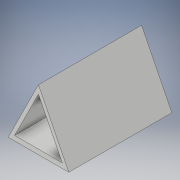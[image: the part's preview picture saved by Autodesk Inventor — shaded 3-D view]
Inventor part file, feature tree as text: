
AUTODESK INVENTOR PART (.ipt)
format: ipt  version: 2019 (Build 230136000, 136)  size: 104,960 bytes
history: native  units: mm
features: extrude x2, sketch x2, other x1
ambient origin geometry x8: Origin, YZ Plane, XZ Plane, XY Plane, X Axis, Y Axis, Z Axis, Center Point
bodies: Body1 (feature_tree)
feature tree (5):
  other  "Sólido1"
  extrude  "Extrusión1"  Depth=50.0mm
  extrude  "Extrusión2"  Depth=3.0mm
  sketch  "Boceto1"  dims[d0=50.0mm d1=50.0mm]
  sketch  "Boceto2"  dims[d2=85.0mm d3=0.0mm d4=3.0mm d5=3.0mm d6=3.0mm d7=85.0mm d8=0.0mm]
